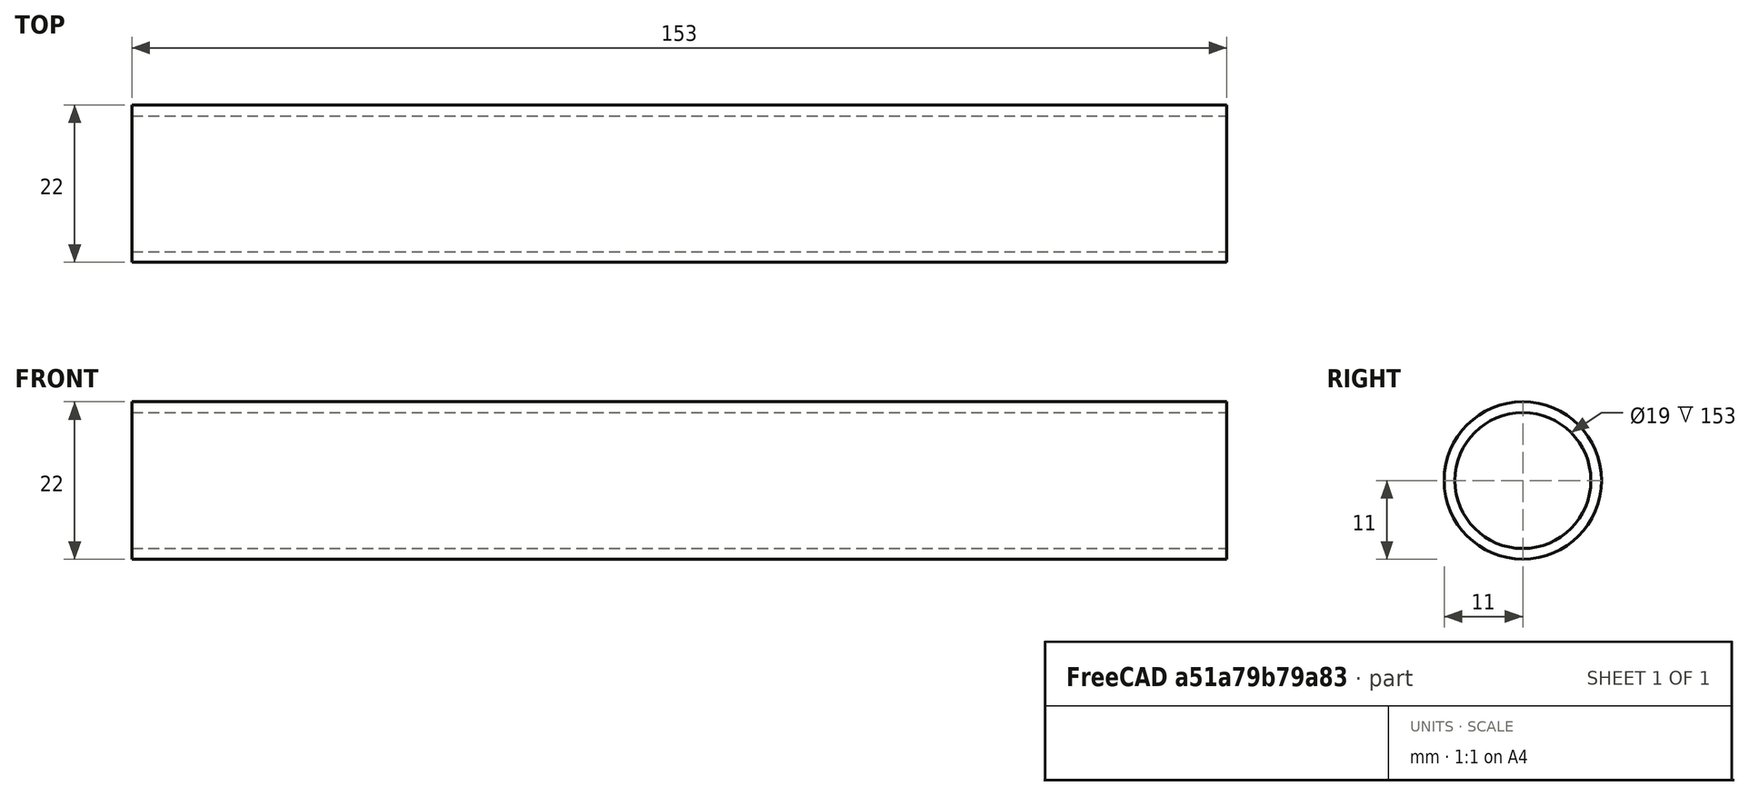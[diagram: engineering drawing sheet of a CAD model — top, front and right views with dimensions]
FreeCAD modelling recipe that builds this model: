
FCSTD DOCUMENT  (FreeCAD 0.17R13541 (Git))
Label: ERG-T-01-ST
License: All rights reserved
LicenseURL: http://en.wikipedia.org/wiki/All_rights_reserved
objects: Drawing::FeatureViewPython×5, Drawing::FeatureViewPart×3, Part::Cylinder×2, Part::Cut×1, Drawing::FeaturePage×1
note: 3 computed .brp shape members not serialized (recipe doc carries the construction recipe); baked Part::Feature solids carry a one-line shape summary decoded from their .brp

FEATURE [Part::Cylinder] Cylinder002  label="INT001"
  Angle = 360
  AttacherType = Attacher::AttachEngine3D
  Height = 153
  Placement = pos=(0,0,2.5) rot=(0,0,1;0rad)
  Radius = 9.5
FEATURE [Part::Cylinder] Cylinder003  label="EXT001"
  Angle = 360
  AttacherType = Attacher::AttachEngine3D
  Height = 153
  Placement = pos=(0,0,2.5) rot=(0,0,1;0rad)
  Radius = 11
FEATURE [Part::Cut] Cut001  label="SteelTube"
  Base = -> Cylinder003
  Placement = pos=(0,0,0) rot=(0,1,0;1.5708rad)
  Refine = true
  Tool = -> Cylinder002
FEATURE [Drawing::FeatureViewPython] dim002  # drawing view (typed FeaturePython)
  Rotation = 0
  ViewResult = <g> \n  <line x1="98.447000" y1="72.000000" x2="93.808261" y2="72.000000" style="stroke:rgb(255,0,0);stroke-width:0.10" />\n<line x1="98.447000" y1="91.000000" x2="93.808261" y2="91.000000" style="stroke:rgb(255,0,0);stroke-width:0.10" />\n<line x1="94.808261" y1="72.000000" x2="94.808261" y2="91.000000" style="stroke:rgb(255,0,0);stroke-width:0.10" /> \n  <polygon points="94.808261,91.000000 95.308261,89.000000 94.808261,88.500000 94.308261,89.000000" style="fill:rgb(255,0,0);stroke:rgb(255,0,0);stroke-width:0" /><polygon points="94.808261,72.000000 94.308261,74.000000 94.808261,74.500000 95.308261,74.000000" style="fill:rgb(255,0,0);stroke:rgb(255,0,0);stroke-width:0" /> \n  <text x="92.808261" y="81.500000" font-family="inherit" font-size="3.6" fill="rgb(0,0,0)" text-anchor="middle" transform="rotate(-90.000000 92.808261,81.500000)" >19</text> </g>
  Visible = false
  X = 0
  Y = 0
  arrowL1 = 2
  arrowL2 = 0.5
  arrowW = 1
  arrow_scheme = 0
  autoPlaceOffset = 2
  autoPlaceText = true
  click1_x = 94.8083
  click1_y = 91.3504
  click2_x = 94.8083
  click2_y = 91.3504
  comma_decimal_place = false
  dimension_line_overshoot = 1
  gap_datum_points = 0
  halfDimension_linear = false
  lineColor = rgb(255,0,0)
  strokeWidth = 0.1
  textFormat_linear = %(value)3.3f
  textRenderer_color = rgb(0,0,0)
  textRenderer_family = inherit
  textRenderer_size = 3.6
  unit_custom_scale = 1
  unit_scheme = 1
FEATURE [Drawing::FeatureViewPython] dim003  # drawing view (typed FeaturePython)
  Rotation = 0
  ViewResult = <g> \n  <line x1="98.447000" y1="92.500000" x2="98.447000" y2="101.835532" style="stroke:rgb(255,0,0);stroke-width:0.10" />\n<line x1="251.447000" y1="92.500000" x2="251.447000" y2="101.835532" style="stroke:rgb(255,0,0);stroke-width:0.10" />\n<line x1="98.447000" y1="100.835532" x2="251.447000" y2="100.835532" style="stroke:rgb(255,0,0);stroke-width:0.10" /> \n  <polygon points="251.447000,100.835532 249.447000,100.335532 248.947000,100.835532 249.447000,101.335532" style="fill:rgb(255,0,0);stroke:rgb(255,0,0);stroke-width:0" /><polygon points="98.447000,100.835532 100.447000,101.335532 100.947000,100.835532 100.447000,100.335532" style="fill:rgb(255,0,0);stroke:rgb(255,0,0);stroke-width:0" /> \n  <text x="174.947000" y="98.835532" font-family="inherit" font-size="3.6" fill="rgb(0,0,0)" text-anchor="middle" transform="rotate(0.000000 174.947000,98.835532)" >153</text> </g>
  Visible = false
  X = 0
  Y = 0
  arrowL1 = 2
  arrowL2 = 0.5
  arrowW = 1
  arrow_scheme = 0
  autoPlaceOffset = 2
  autoPlaceText = true
  click1_x = 228.521
  click1_y = 100.836
  click2_x = 228.521
  click2_y = 100.836
  comma_decimal_place = false
  dimension_line_overshoot = 1
  gap_datum_points = 0
  halfDimension_linear = false
  lineColor = rgb(255,0,0)
  strokeWidth = 0.1
  textFormat_linear = %(value)3.3f
  textRenderer_color = rgb(0,0,0)
  textRenderer_family = inherit
  textRenderer_size = 3.6
  unit_custom_scale = 1
  unit_scheme = 1
FEATURE [Drawing::FeatureViewPart] Ortho  label="Ortho_0_0"
  Direction = (1,0,0)
  HiddenWidth = 0.15
  LineWidth = 0.35
  Rotation = -90
  ShowHiddenLines = true
  ShowSmoothLines = false
  Source = -> Cut001
  Tolerance = 0.05
  ViewResult = <g id="Ortho_0_0"\n   transform="rotate(-90,53.9733,81.5) translate(53.9733,81.5) scale(1,1)"\n  >\n<g   fill="none"\n   stroke="rgb(0, 0, 0)"\n   stroke-dasharray="0.2,0.1)"\n   stroke-linecap="butt"\n   stroke-linejoin="miter"\n   stroke-width="0.150000"\n   transform="scale(1,-1)"\n  >\n<circle cx ="5.55112e-16" cy ="0" r ="11" /><circle cx ="5.55112e-16" cy ="0" r ="9.5" /></g>\n<g   fill="none"\n   stroke="rgb(0, 0, 0)"\n   stroke-linecap="butt"\n   stroke-linejoin="miter"\n   stroke-width="0.350000"\n   transform="scale(1,-1)"\n  >\n<circle cx ="3.45279e-14" cy ="0" r ="11" /><circle cx ="3.45279e-14" cy ="0" r ="9.5" /></g>\n</g>
  Visible = false
  X = 53.9733
  Y = 81.5
FEATURE [Drawing::FeatureViewPart] Ortho001  label="Ortho_1_0"
  Direction = (0,1,0)
  HiddenWidth = 0.15
  LineWidth = 0.35
  Rotation = -90
  ShowHiddenLines = true
  ShowSmoothLines = false
  Source = -> Cut001
  Tolerance = 0.05
  ViewResult = <blob: 2833 chars omitted>
  Visible = false
  X = 253.947
  Y = 81.5
FEATURE [Drawing::FeatureViewPython] dim001  # drawing view (typed FeaturePython)
  Rotation = 0
  ViewResult = <g> \n  <line x1="98.447000" y1="70.500000" x2="87.594019" y2="70.500000" style="stroke:rgb(255,0,0);stroke-width:0.10" />\n<line x1="98.447000" y1="92.500000" x2="87.594019" y2="92.500000" style="stroke:rgb(255,0,0);stroke-width:0.10" />\n<line x1="88.594019" y1="70.500000" x2="88.594019" y2="92.500000" style="stroke:rgb(255,0,0);stroke-width:0.10" /> \n  <polygon points="88.594019,92.500000 89.094019,90.500000 88.594019,90.000000 88.094019,90.500000" style="fill:rgb(255,0,0);stroke:rgb(255,0,0);stroke-width:0" /><polygon points="88.594019,70.500000 88.094019,72.500000 88.594019,73.000000 89.094019,72.500000" style="fill:rgb(255,0,0);stroke:rgb(255,0,0);stroke-width:0" /> \n  <text x="86.594019" y="81.500000" font-family="inherit" font-size="3.6" fill="rgb(0,0,0)" text-anchor="middle" transform="rotate(-90.000000 86.594019,81.500000)" >22</text> </g>
  Visible = false
  X = 0
  Y = 0
  arrowL1 = 2
  arrowL2 = 0.5
  arrowW = 1
  arrow_scheme = 0
  autoPlaceOffset = 2
  autoPlaceText = true
  click1_x = 88.594
  click1_y = 93.4542
  click2_x = 88.594
  click2_y = 93.4542
  comma_decimal_place = false
  dimension_line_overshoot = 1
  gap_datum_points = 0
  halfDimension_linear = false
  lineColor = rgb(255,0,0)
  strokeWidth = 0.1
  textFormat_linear = %(value)3.3f
  textRenderer_color = rgb(0,0,0)
  textRenderer_family = inherit
  textRenderer_size = 3.6
  unit_custom_scale = 1
  unit_scheme = 1
FEATURE [Drawing::FeatureViewPython] dia002  # drawing view (typed FeaturePython)
  Rotation = 0
  ViewResult = <g>  <circle cx ="53.973300" cy ="81.500000" r="0.250000" stroke="none" fill="rgb(255,0,0)" /> \n<line x1="70.619025" y1="103.897032" x2="48.306482" y2="73.875226" style="stroke:rgb(255,0,0);stroke-width:0.10" />\n<polygon points="59.640118,89.124774 58.848407,87.221305 58.148850,87.118255 58.045799,87.817812" style="fill:rgb(255,0,0);stroke:rgb(255,0,0);stroke-width:0" />\n<polygon points="48.306482,73.875226 49.098193,75.778695 49.797750,75.881745 49.900801,75.182188" style="fill:rgb(255,0,0);stroke:rgb(255,0,0);stroke-width:0" />\n<line x1="70.619025" y1="103.897032" x2="80.937787" y2="103.897032" style="stroke:rgb(255,0,0);stroke-width:0.10" />\n<text x="75.778406" y="101.897032" font-family="inherit" font-size="3.6" fill="rgb(0,0,0)" text-anchor="middle" transform="rotate(0.000000 75.778406,101.897032)" >Ø19</text> </g>
  Visible = false
  X = 0
  Y = 0
  arrowL1 = 2
  arrowL2 = 0.5
  arrowW = 1
  arrow_scheme = 0
  autoPlaceOffset = 2
  autoPlaceText = true
  centerPointDia = 0.5
  click1_x = 70.619
  click1_y = 103.897
  click2_x = 80.9378
  click2_y = 104.026
  click3_x = 80.9378
  click3_y = 104.026
  comma_decimal_place = false
  lineColor = rgb(255,0,0)
  strokeWidth = 0.1
  textFormat_circular = Ø%(value)3.3f
  textRenderer_color = rgb(0,0,0)
  textRenderer_family = inherit
  textRenderer_size = 3.6
  unit_custom_scale = 1
  unit_scheme = 1
FEATURE [Drawing::FeatureViewPart] View
  Direction = (0,0,1)
  HiddenWidth = 0.15
  LineWidth = 0.35
  Rotation = 0
  ShowHiddenLines = false
  ShowSmoothLines = false
  Tolerance = 0.05
  ViewResult = <blob: 4585 chars omitted>
  Visible = false
  X = 10
  Y = 10
FEATURE [Drawing::FeatureViewPython] dia001  # drawing view (typed FeaturePython)
  Rotation = 0
  ViewResult = <g>  <circle cx ="53.973300" cy ="81.500000" r="0.250000" stroke="none" fill="rgb(255,0,0)" /> \n<line x1="43.793842" y1="112.648900" x2="57.390264" y2="71.044171" style="stroke:rgb(255,0,0);stroke-width:0.10" />\n<polygon points="50.556336,91.955829 51.652867,90.210086 51.332919,89.579504 50.702337,89.899453" style="fill:rgb(255,0,0);stroke:rgb(255,0,0);stroke-width:0" />\n<polygon points="57.390264,71.044171 56.293733,72.789914 56.613681,73.420496 57.244263,73.100547" style="fill:rgb(255,0,0);stroke:rgb(255,0,0);stroke-width:0" />\n<line x1="43.793842" y1="112.648900" x2="32.908667" y2="112.648900" style="stroke:rgb(255,0,0);stroke-width:0.10" />\n<text x="38.351255" y="110.648900" font-family="inherit" font-size="3.6" fill="rgb(0,0,0)" text-anchor="middle" transform="rotate(0.000000 38.351255,110.648900)" >Ø22</text> </g>
  Visible = false
  X = 0
  Y = 0
  arrowL1 = 2
  arrowL2 = 0.5
  arrowW = 1
  arrow_scheme = 0
  autoPlaceOffset = 2
  autoPlaceText = true
  centerPointDia = 0.5
  click1_x = 43.7938
  click1_y = 112.649
  click2_x = 32.9087
  click2_y = 117.205
  click3_x = 32.9087
  click3_y = 117.205
  comma_decimal_place = false
  lineColor = rgb(255,0,0)
  strokeWidth = 0.1
  textFormat_circular = Ø%(value)3.3f
  textRenderer_color = rgb(0,0,0)
  textRenderer_family = inherit
  textRenderer_size = 3.6
  unit_custom_scale = 1.7
  unit_scheme = 0
FEATURE [Drawing::FeaturePage] Page  label="Steel Tube"
  EditableTexts = Dr. Zoidberg | 05.02.2019 | x1.0 | unknown | ERG-T-01 | Steel Tube 2 | 07 | 07
  Group = -> [Ortho,Ortho001,dim001,dim002,dim003,dia002,View,dia001]
  Template = <path>//share/freecad/Mod/Drawing/Templates/A4_Landscape.svg
note: 1 file-system path scrubbed to <path> (originals preserved in the JSON sidecar)
